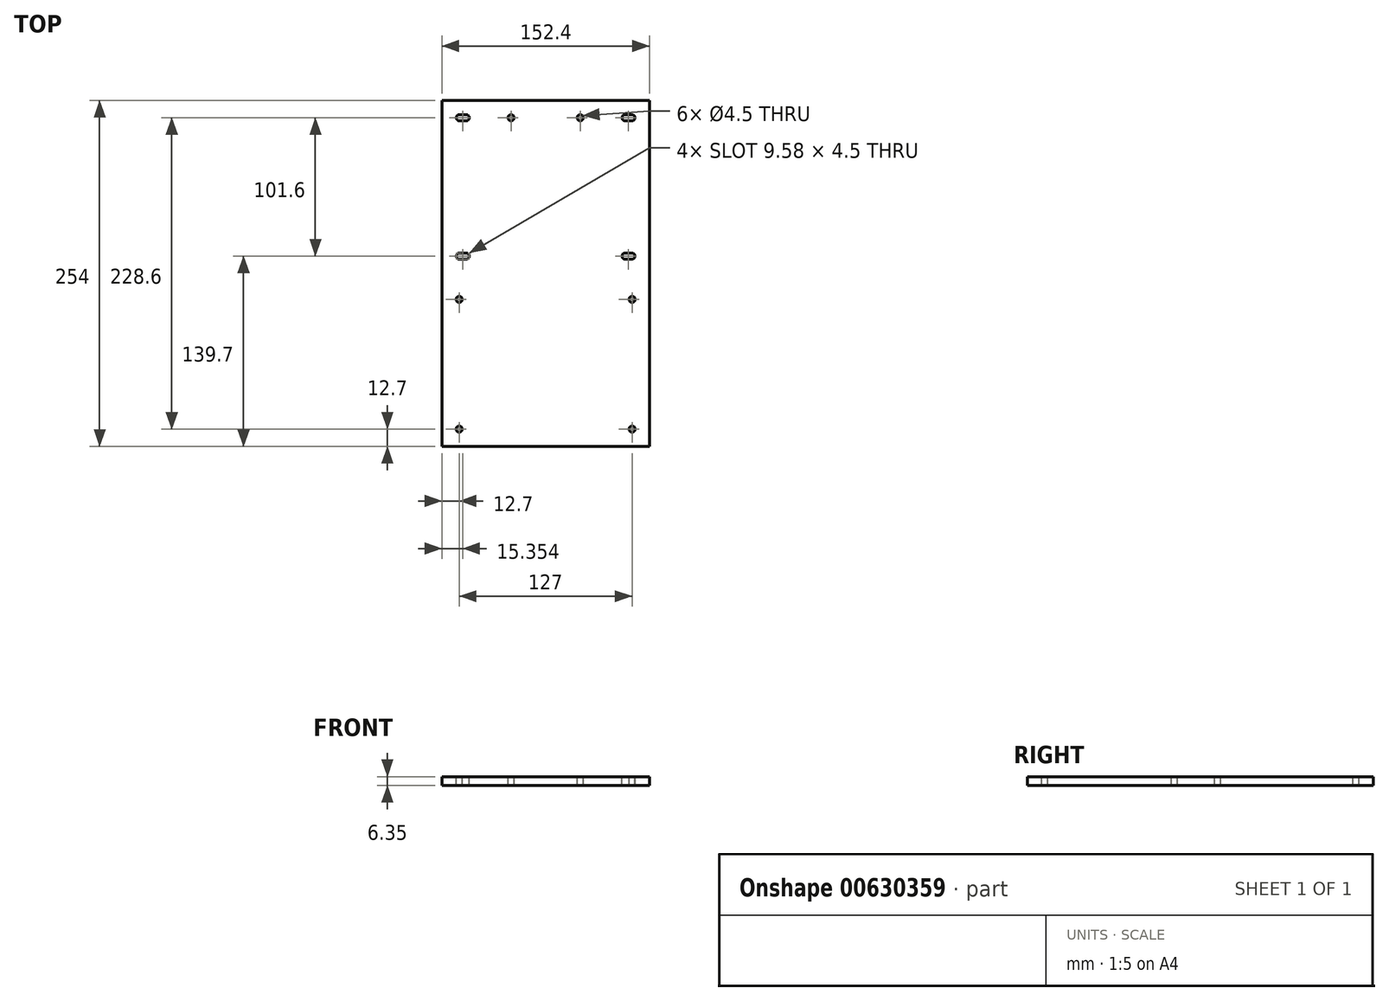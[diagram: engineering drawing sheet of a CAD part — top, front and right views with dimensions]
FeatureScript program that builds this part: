
annotation { "Feature Type Name" : "Feature", "Feature Type Description" : "" }
export const myFeature = defineFeature(function(context is Context, id is Id, definition is map)
    precondition{}
    {
        {
            var Q0;
            Q0=qCreatedBy(makeId("Top.planeOp"),FACE);
            var sketch = newSketch(context, id + "F0", { "sketchPlane" : qUnion([Q0])});
            skLineSegment(sketch, "E0.bottom", {"start": v(-76.2, 127) * mm, "end": v(76.2, 127) * mm});
            skLineSegment(sketch, "E0.top", {"start": v(-76.2, -127) * mm, "end": v(76.2, -127) * mm});
            skLineSegment(sketch, "E0.left", {"start": v(-76.2, 127) * mm, "end": v(-76.2, -127) * mm});
            skLineSegment(sketch, "E0.right", {"start": v(76.2, 127) * mm, "end": v(76.2, -127) * mm});
            skPoint(sketch, "E0.middle", {"position": v(0, 0) * mm});
            skSolve(sketch);
        }
        {
            var Q0;
            Q0 = qSketchRegion(id + "F0", true);
            extrude(context, id + "F1", {"entities" : qUnion([Q0]), "depth" : 6.35 * mm, "offsetDistance" : 25.4 * mm});
        }
        {
            var Q0;
            Q0=makeQuery(id+"F1.opExtrude","CAP_FACE",FACE,{"disambiguationData":[OSD([sQuery(id+"F0.wireOp",EDGE,"E0.bottom"),sQuery(id+"F0.wireOp",EDGE,"E0.top"),sQuery(id+"F0.wireOp",EDGE,"E0.left"),sQuery(id+"F0.wireOp",EDGE,"E0.right")])],"isStart":false});
            var sketch = newSketch(context, id + "F2", { "sketchPlane" : qUnion([Q0])});
            skLineSegment(sketch, "E1.bottom", {"start": v(-63.39, 116.55) * mm, "end": v(-58.3, 116.55) * mm});
            skLineSegment(sketch, "E1.top", {"start": v(-63.39, 112.05) * mm, "end": v(-58.3, 112.05) * mm});
            skLineSegment(sketch, "E1.left", {"start": v(-63.39, 116.55) * mm, "end": v(-63.39, 112.05) * mm, "construction": true});
            skLineSegment(sketch, "E1.right", {"start": v(-58.3, 116.55) * mm, "end": v(-58.3, 112.05) * mm, "construction": true});
            skArc(sketch, "E2", {"start": v(-63.39, 116.55) * mm, "mid": v(-65.63, 114.3) * mm, "end": v(-63.39, 112.05) * mm});
            skArc(sketch, "E3", {"start": v(-58.3, 116.55) * mm, "mid": v(-56.06, 114.3) * mm, "end": v(-58.3, 112.05) * mm});
            skLineSegment(sketch, "E4", {"start": v(-63.39, 116.55) * mm, "end": v(-58.3, 112.05) * mm, "construction": true});
            skPoint(sketch, "E5", {"position": v(-60.85, 114.3) * mm});
            skLineSegment(sketch, "E6.bottom", {"start": v(58.3, 116.55) * mm, "end": v(63.39, 116.55) * mm});
            skLineSegment(sketch, "E6.top", {"start": v(58.3, 112.05) * mm, "end": v(63.39, 112.05) * mm});
            skLineSegment(sketch, "E6.left", {"start": v(58.3, 116.55) * mm, "end": v(58.3, 112.05) * mm, "construction": true});
            skLineSegment(sketch, "E6.right", {"start": v(63.39, 116.55) * mm, "end": v(63.39, 112.05) * mm, "construction": true});
            skArc(sketch, "E7", {"start": v(58.3, 116.55) * mm, "mid": v(56.06, 114.3) * mm, "end": v(58.3, 112.05) * mm});
            skArc(sketch, "E8", {"start": v(63.39, 116.55) * mm, "mid": v(65.63, 114.3) * mm, "end": v(63.39, 112.05) * mm});
            skLineSegment(sketch, "E9", {"start": v(58.3, 116.55) * mm, "end": v(63.39, 112.05) * mm, "construction": true});
            skPoint(sketch, "E10", {"position": v(60.85, 114.3) * mm});
            skLineSegment(sketch, "E11.bottom", {"start": v(-63.39, 14.95) * mm, "end": v(-58.3, 14.95) * mm});
            skLineSegment(sketch, "E11.top", {"start": v(-63.39, 10.45) * mm, "end": v(-58.3, 10.45) * mm});
            skLineSegment(sketch, "E11.left", {"start": v(-63.39, 14.95) * mm, "end": v(-63.39, 10.45) * mm, "construction": true});
            skLineSegment(sketch, "E11.right", {"start": v(-58.3, 14.95) * mm, "end": v(-58.3, 10.45) * mm, "construction": true});
            skArc(sketch, "E12", {"start": v(-63.39, 14.95) * mm, "mid": v(-65.63, 12.7) * mm, "end": v(-63.39, 10.45) * mm});
            skArc(sketch, "E13", {"start": v(-58.3, 14.95) * mm, "mid": v(-56.06, 12.7) * mm, "end": v(-58.3, 10.45) * mm});
            skLineSegment(sketch, "E14", {"start": v(-63.39, 14.95) * mm, "end": v(-58.3, 10.45) * mm, "construction": true});
            skPoint(sketch, "E15", {"position": v(-60.85, 12.7) * mm});
            skLineSegment(sketch, "E16.bottom", {"start": v(58.3, 14.95) * mm, "end": v(63.39, 14.95) * mm});
            skLineSegment(sketch, "E16.top", {"start": v(58.3, 10.45) * mm, "end": v(63.39, 10.45) * mm});
            skLineSegment(sketch, "E16.left", {"start": v(58.3, 14.95) * mm, "end": v(58.3, 10.45) * mm, "construction": true});
            skLineSegment(sketch, "E16.right", {"start": v(63.39, 14.95) * mm, "end": v(63.39, 10.45) * mm, "construction": true});
            skArc(sketch, "E17", {"start": v(58.3, 14.95) * mm, "mid": v(56.06, 12.7) * mm, "end": v(58.3, 10.45) * mm});
            skArc(sketch, "E18", {"start": v(63.39, 14.95) * mm, "mid": v(65.63, 12.7) * mm, "end": v(63.39, 10.45) * mm});
            skLineSegment(sketch, "E19", {"start": v(58.3, 14.95) * mm, "end": v(63.39, 10.45) * mm, "construction": true});
            skPoint(sketch, "E20", {"position": v(60.85, 12.7) * mm});
            skLineSegment(sketch, "E21.bottom", {"start": v(-60.85, 114.3) * mm, "end": v(60.85, 114.3) * mm, "construction": true});
            skLineSegment(sketch, "E21.top", {"start": v(-60.85, 12.7) * mm, "end": v(60.85, 12.7) * mm, "construction": true});
            skLineSegment(sketch, "E21.left", {"start": v(-60.85, 114.3) * mm, "end": v(-60.85, 12.7) * mm, "construction": true});
            skLineSegment(sketch, "E21.right", {"start": v(60.85, 114.3) * mm, "end": v(60.85, 12.7) * mm, "construction": true});
            skLineSegment(sketch, "E22", {"start": v(0, 114.3) * mm, "end": v(0, 127) * mm, "construction": true});
            skSolve(sketch);
        }
        {
            var Q0;
            Q0 = qSketchRegion(id + "F2", true);
            extrude(context, id + "F3", {"entities" : qUnion([Q0]), "operationType" : NewBodyOperationType.REMOVE, "oppositeDirection" : true, "depth" : 25.4 * mm, "offsetDistance" : 25.4 * mm});
        }
        {
            var Q0;
            Q0=makeQuery(id+"F2.imprint","IMPRINT",FACE,{"disambiguationData":[TD([[makeQuery(id+"F2.imprint","IMPRINT",EDGE,{"derivedFrom":sQuery(id+"F2.wireOp",EDGE,"E1.bottom")}),1.0]])]});
            var sketch = newSketch(context, id + "F4", { "sketchPlane" : qUnion([Q0])});
            skPoint(sketch, "E23", {"position": v(60.85, 114.3) * mm});
            skSolve(sketch);
        }
        {
            var Q0;
            Q0=makeQuery(id+"F4.imprint","IMPRINT",FACE,{"disambiguationData":[TD([[makeQuery(id+"F4.imprint","IMPRINT",EDGE,{"derivedFrom":makeQuery(id+"F2.imprint","IMPRINT",EDGE,{"derivedFrom":sQuery(id+"F2.wireOp",EDGE,"E1.bottom")})}),1.0]])]});
            var sketch = newSketch(context, id + "F5", { "sketchPlane" : qUnion([Q0])});
            skLineSegment(sketch, "E24.bottom", {"start": v(-63.5, -114.3) * mm, "end": v(63.5, -114.3) * mm, "construction": true});
            skLineSegment(sketch, "E24.top", {"start": v(-63.5, -19.05) * mm, "end": v(63.5, -19.05) * mm, "construction": true});
            skLineSegment(sketch, "E24.left", {"start": v(-63.5, -114.3) * mm, "end": v(-63.5, -19.05) * mm, "construction": true});
            skLineSegment(sketch, "E24.right", {"start": v(63.5, -114.3) * mm, "end": v(63.5, -19.05) * mm, "construction": true});
            skLineSegment(sketch, "E25", {"start": v(0, 0) * mm, "end": v(0, -66.67) * mm, "construction": true});
            skLineSegment(sketch, "E26", {"start": v(63.5, -114.3) * mm, "end": v(-63.5, -19.05) * mm, "construction": true});
            skPoint(sketch, "E27", {"position": v(-63.5, -19.05) * mm});
            skPoint(sketch, "E28", {"position": v(-63.5, -114.3) * mm});
            skPoint(sketch, "E29", {"position": v(63.5, -114.3) * mm});
            skPoint(sketch, "E30", {"position": v(63.5, -19.05) * mm});
            skPoint(sketch, "E31", {"position": v(-25.4, 114.3) * mm});
            skPoint(sketch, "E32", {"position": v(25.4, 114.3) * mm});
            skLineSegment(sketch, "E33", {"start": v(0, 0) * mm, "end": v(0, 114.3) * mm, "construction": true});
            skLineSegment(sketch, "E34", {"start": v(-25.4, 114.3) * mm, "end": v(25.4, 114.3) * mm, "construction": true});
            skSolve(sketch);
        }
        {
            var Q0;
            Q0=sQuery(id+"F5.wireOp",VERTEX,"E27");
            var Q1;
            Q1=sQuery(id+"F5.wireOp",VERTEX,"E28");
            var Q2;
            Q2=sQuery(id+"F5.wireOp",VERTEX,"E29");
            var Q3;
            Q3=sQuery(id+"F5.wireOp",VERTEX,"E30");
            var Q4;
            Q4=sQuery(id+"F5.wireOp",VERTEX,"E31");
            var Q5;
            Q5=sQuery(id+"F5.wireOp",VERTEX,"E32");
            var Q6;
            Q6=makeQuery(id+"F1.opExtrude","SWEPT_BODY",BODY,{"disambiguationData":[OSD([sQuery(id+"F0.wireOp",EDGE,"E0.bottom"),sQuery(id+"F0.wireOp",EDGE,"E0.top"),sQuery(id+"F0.wireOp",EDGE,"E0.left"),sQuery(id+"F0.wireOp",EDGE,"E0.right")])]});
            hole(context, id + "F6", {"style" : HoleStyle.SIMPLE, "endStyle" : HoleEndStyle.THROUGH, "standardTappedOrClearance" : lookupTablePath({ "standard" : "ANSI", "fit" : "Normal (ASME)", "size" : "#8", "type" : "Clearance" }), "standardBlindInLast" : lookupTablePath({ "fit" : "Free", "standard" : "ANSI", "size" : "#8", "type" : "Clearance" }), "holeDiameter" : 4.5 * mm, "majorDiameter" : 6.35 * mm, "isTappedThrough" : true, "tappedDepth" : 12.7 * mm, "tapClearance" : 3, "locations" : qUnion([Q0, Q1, Q2, Q3, Q4, Q5]), "scope" : qUnion([Q6])});
        }
    });
